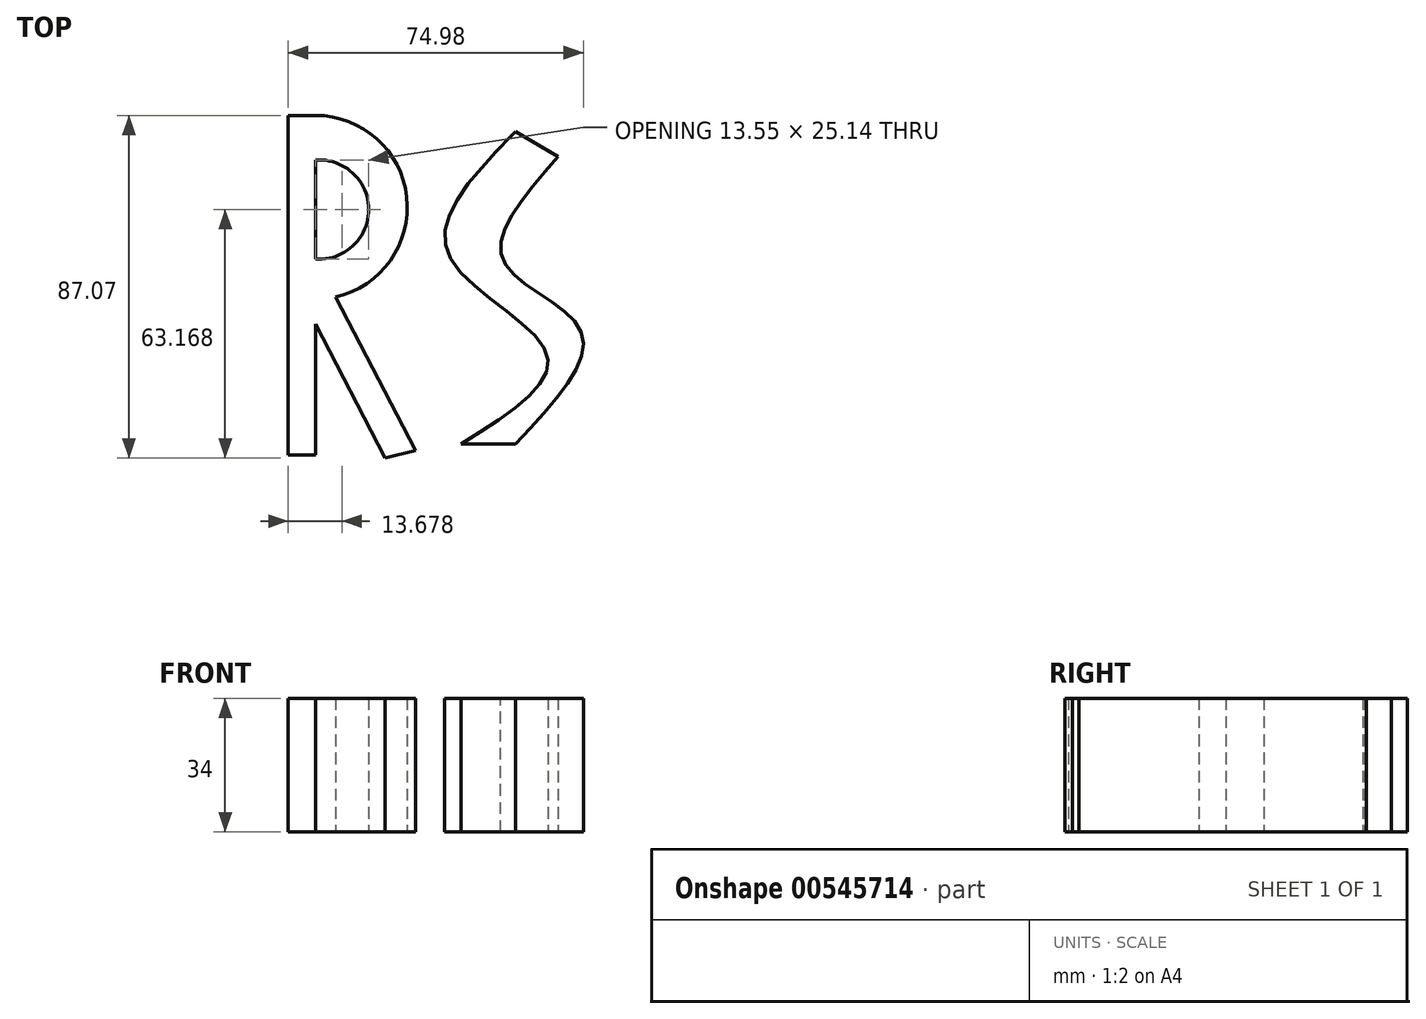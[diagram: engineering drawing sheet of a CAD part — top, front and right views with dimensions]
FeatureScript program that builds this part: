
annotation { "Feature Type Name" : "Feature", "Feature Type Description" : "" }
export const myFeature = defineFeature(function(context is Context, id is Id, definition is map)
    precondition{}
    {
        {
            var Q0;
            Q0=qCreatedBy(makeId("Top.planeOp"),FACE);
            var sketch = newSketch(context, id + "F0", { "sketchPlane" : qUnion([Q0])});
            skLineSegment(sketch, "E0.bottom", {"start": v(-65.76, 39.79) * mm, "end": v(-58.86, 39.79) * mm});
            skLineSegment(sketch, "E0.top", {"start": v(-65.76, -46.42) * mm, "end": v(-58.86, -46.42) * mm});
            skLineSegment(sketch, "E0.left", {"start": v(-65.76, 39.79) * mm, "end": v(-65.76, -46.42) * mm});
            skLineSegment(sketch, "E0.right", {"start": v(-58.86, 39.79) * mm, "end": v(-58.86, -46.42) * mm});
            skArc(sketch, "E1", {"start": v(-58.86, -6.9) * mm, "mid": v(-35.5, 16.44) * mm, "end": v(-58.86, 39.79) * mm});
            skLineSegment(sketch, "E2", {"start": v(-53.68, -6.33) * mm, "end": v(-33.43, -45.32) * mm});
            skLineSegment(sketch, "E3", {"start": v(-33.43, -45.32) * mm, "end": v(-53.68, -6.33) * mm});
            skLineSegment(sketch, "E4", {"start": v(-58.86, -13.26) * mm, "end": v(-41.19, -47.28) * mm});
            skLineSegment(sketch, "E5", {"start": v(-41.19, -47.28) * mm, "end": v(-33.43, -45.32) * mm});
            skFitSpline(sketch, "E6", {"points": [v(-8.01, 35.64) * mm, v(-25.14, 4.7) * mm, v(0, -21) * mm, v(-21.83, -43.66) * mm], "startDerivative": vector(-93.38, -95.33) * mm, "endDerivative": vector(-113.04, -70.83) * mm});
            skFitSpline(sketch, "E7", {"points": [v(2.76, 29.29) * mm, v(-11.05, 2.76) * mm, v(8.57, -14.92) * mm, v(-8.01, -43.66) * mm], "startDerivative": vector(-76.8, -87.33) * mm, "endDerivative": vector(-84.87, -90.33) * mm});
            skLineSegment(sketch, "E8", {"start": v(-8.99, 34.65) * mm, "end": v(-8.01, 35.64) * mm});
            skLineSegment(sketch, "E9", {"start": v(-8.01, 35.64) * mm, "end": v(2.76, 29.29) * mm});
            skLineSegment(sketch, "E10", {"start": v(-21.83, -43.66) * mm, "end": v(-8.01, -43.66) * mm});
            skArc(sketch, "E11", {"start": v(-58.86, 3.32) * mm, "mid": v(-45.3, 15.89) * mm, "end": v(-58.86, 28.46) * mm});
            skLineSegment(sketch, "E12", {"start": v(-58.86, 28.46) * mm, "end": v(-58.86, 3.32) * mm});
            skSolve(sketch);
        }
        {
            var Q0;
            Q0 = qSketchRegion(id + "F0", true);
            extrude(context, id + "F1", {"entities" : qUnion([Q0]), "depth" : 34 * mm, "offsetDistance" : 25 * mm});
        }
    });
